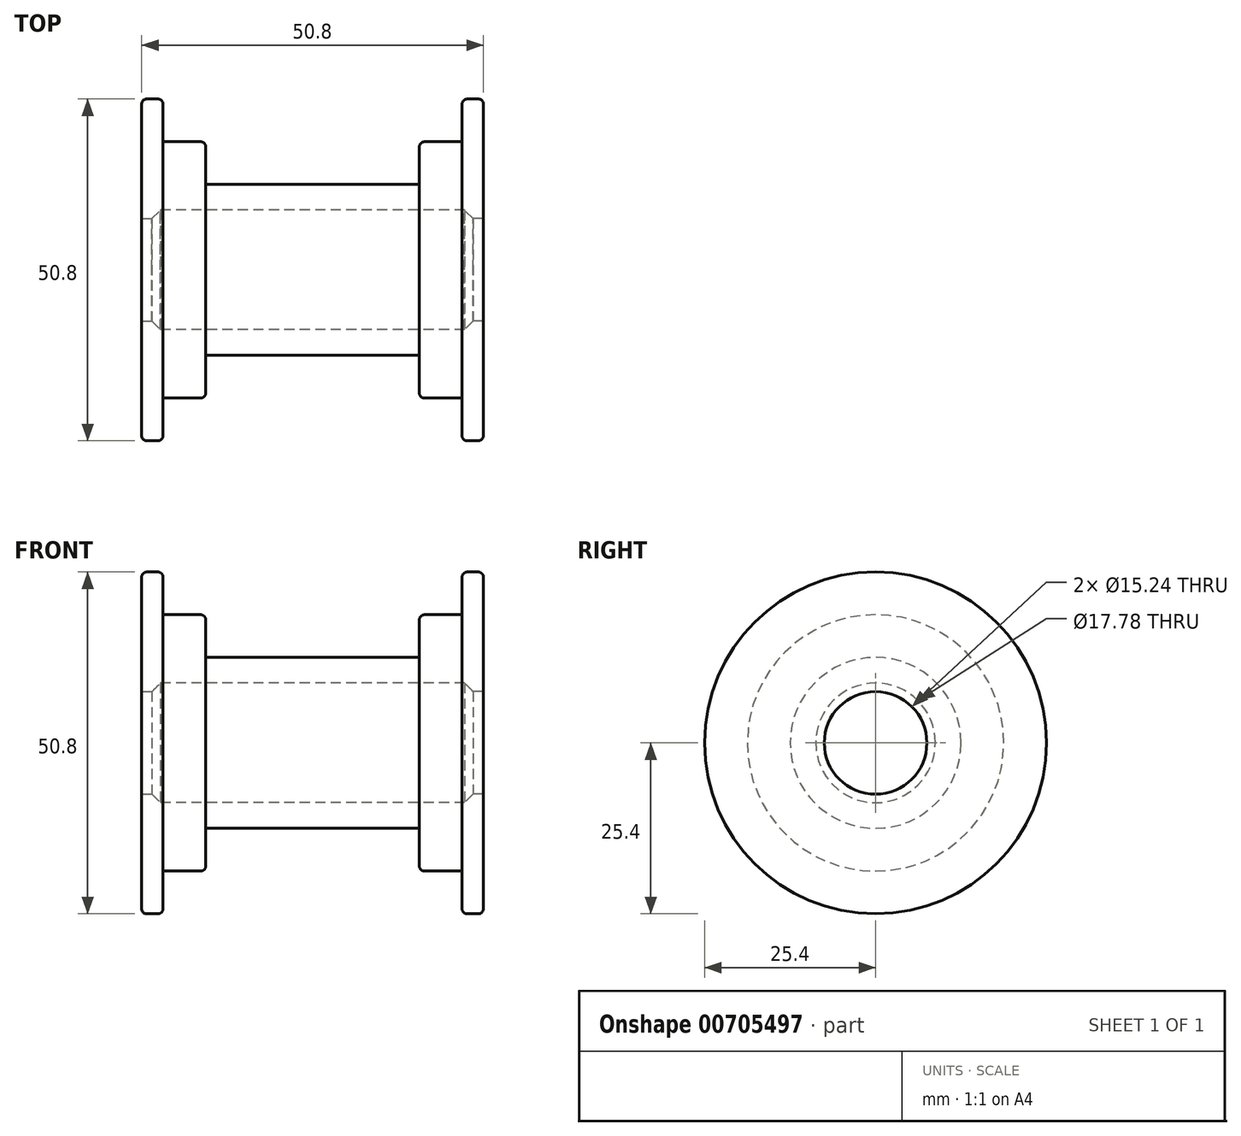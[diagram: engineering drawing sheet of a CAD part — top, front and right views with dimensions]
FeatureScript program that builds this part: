
annotation { "Feature Type Name" : "Feature", "Feature Type Description" : "" }
export const myFeature = defineFeature(function(context is Context, id is Id, definition is map)
    precondition{}
    {
        {
            var Q0;
            Q0=qCreatedBy(makeId("Top.planeOp"),FACE);
            var sketch = newSketch(context, id + "F0", { "sketchPlane" : qUnion([Q0])});
            skLineSegment(sketch, "E0", {"start": v(1.1, 0) * mm, "end": v(48.2, 0) * mm, "construction": true});
            skLineSegment(sketch, "E1", {"start": v(0, 0) * mm, "end": v(0, 33.23) * mm, "construction": true});
            skLineSegment(sketch, "E2", {"start": v(0, 12.7) * mm, "end": v(15.88, 12.7) * mm});
            skLineSegment(sketch, "E3", {"start": v(15.88, 12.7) * mm, "end": v(15.88, 18.29) * mm});
            skLineSegment(sketch, "E4", {"start": v(16.64, 19.05) * mm, "end": v(22.23, 19.05) * mm});
            skLineSegment(sketch, "E5", {"start": v(22.23, 19.05) * mm, "end": v(22.23, 24.64) * mm});
            skLineSegment(sketch, "E6", {"start": v(22.99, 25.4) * mm, "end": v(24.64, 25.4) * mm});
            skLineSegment(sketch, "E7", {"start": v(25.4, 24.64) * mm, "end": v(25.4, 7.62) * mm});
            skLineSegment(sketch, "E8", {"start": v(25.4, 7.62) * mm, "end": v(23.88, 7.62) * mm});
            skLineSegment(sketch, "E9", {"start": v(23.88, 7.62) * mm, "end": v(22.6, 8.9) * mm});
            skLineSegment(sketch, "E10", {"start": v(22.6, 8.9) * mm, "end": v(0, 8.9) * mm});
            skLineSegment(sketch, "E11", {"start": v(0, 8.9) * mm, "end": v(0, 12.7) * mm});
            skPoint(sketch, "E12.visualSharp", {"position": v(15.88, 19.05) * mm});
            skArc(sketch, "E12.filletArc", {"start": v(16.64, 19.05) * mm, "mid": v(16.1, 18.83) * mm, "end": v(15.88, 18.29) * mm});
            skPoint(sketch, "E13.visualSharp", {"position": v(22.23, 25.4) * mm});
            skArc(sketch, "E13.filletArc", {"start": v(22.99, 25.4) * mm, "mid": v(22.45, 25.18) * mm, "end": v(22.23, 24.64) * mm});
            skPoint(sketch, "E14.visualSharp", {"position": v(25.4, 25.4) * mm});
            skArc(sketch, "E14.filletArc", {"start": v(25.4, 24.64) * mm, "mid": v(25.18, 25.18) * mm, "end": v(24.64, 25.4) * mm});
            skSolve(sketch);
        }
        {
            var Q0;
            Q0 = qSketchRegion(id + "F0", true);
            var Q1;
            Q1=sQuery(id+"F0.wireOp",EDGE,"E0");
            revolve(context, id + "F1", {"surfaceOperationType" : NewSurfaceOperationType.NEW, "entities" : qUnion([Q0]), "axis" : qUnion([Q1]), "revolveType" : RevolveType.FULL});
        }
        {
            var Q0;
            Q0=makeQuery(id+"F1.opRevolve","SWEPT_BODY",BODY,{"disambiguationData":[OSD([sQuery(id+"F0.wireOp",EDGE,"E2"),sQuery(id+"F0.wireOp",EDGE,"E3"),sQuery(id+"F0.wireOp",EDGE,"E4"),sQuery(id+"F0.wireOp",EDGE,"E5"),sQuery(id+"F0.wireOp",EDGE,"E6"),sQuery(id+"F0.wireOp",EDGE,"E7"),sQuery(id+"F0.wireOp",EDGE,"E8"),sQuery(id+"F0.wireOp",EDGE,"E9"),sQuery(id+"F0.wireOp",EDGE,"E10"),sQuery(id+"F0.wireOp",EDGE,"E11")])]});
            var Q1;
            Q1=makeQuery(id+"F1.opRevolve","SWEPT_FACE",FACE,{"disambiguationData":[OSD([sQuery(id+"F0.wireOp",EDGE,"E11")])]});
            mirror(context, id + "F2", {"operationType" : NewBodyOperationType.ADD, "entities" : qUnion([Q0]), "mirrorPlane" : qUnion([Q1])});
        }
    });
